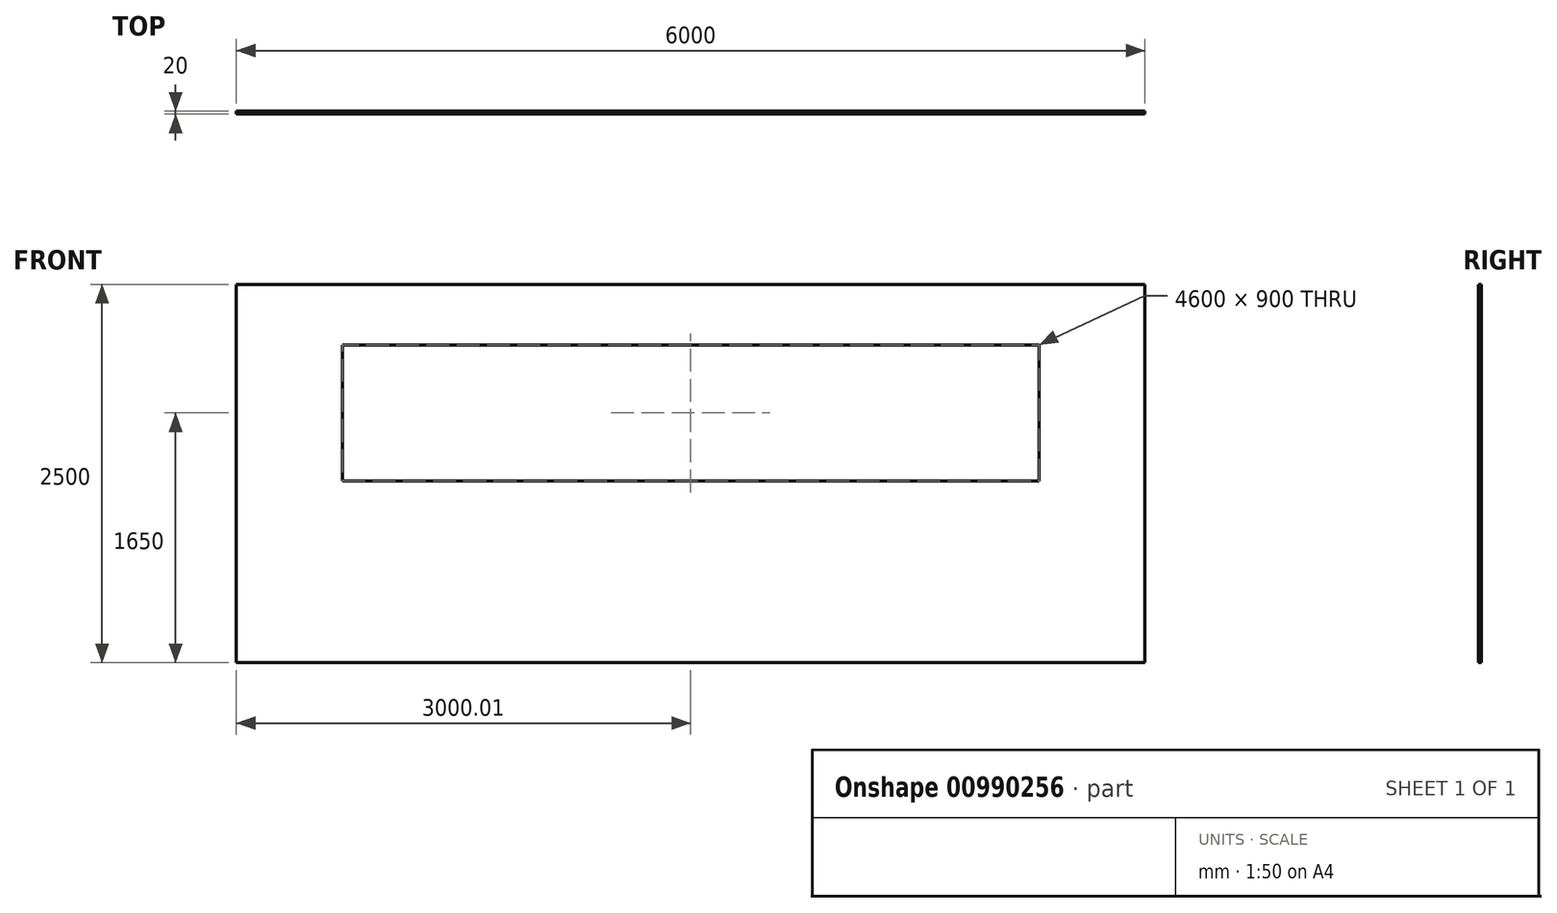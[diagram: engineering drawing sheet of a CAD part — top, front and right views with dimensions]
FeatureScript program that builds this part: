
annotation { "Feature Type Name" : "Feature", "Feature Type Description" : "" }
export const myFeature = defineFeature(function(context is Context, id is Id, definition is map)
    precondition{}
    {
        {
            var Q0;
            Q0=qCreatedBy(makeId("Front.planeOp"),FACE);
            var sketch = newSketch(context, id + "F0", { "sketchPlane" : qUnion([Q0])});
            skLineSegment(sketch, "E0.bottom", {"start": v(3864.31, 1300) * mm, "end": v(-2135.69, 1300) * mm});
            skLineSegment(sketch, "E0.top", {"start": v(3864.31, -1200) * mm, "end": v(-2135.69, -1200) * mm});
            skLineSegment(sketch, "E0.left", {"start": v(3864.31, 1300) * mm, "end": v(3864.31, -1200) * mm});
            skLineSegment(sketch, "E0.right", {"start": v(-2135.69, 1300) * mm, "end": v(-2135.69, -1200) * mm});
            skLineSegment(sketch, "E1.bottom", {"start": v(3164.31, 0) * mm, "end": v(-1435.69, 0) * mm});
            skLineSegment(sketch, "E1.top", {"start": v(3164.31, 900) * mm, "end": v(-1435.69, 900) * mm});
            skLineSegment(sketch, "E1.left", {"start": v(3164.31, 0) * mm, "end": v(3164.31, 900) * mm});
            skLineSegment(sketch, "E1.right", {"start": v(-1435.69, 0) * mm, "end": v(-1435.69, 900) * mm});
            skSolve(sketch);
        }
        {
            var Q0;
            Q0=makeQuery(id+"F0.imprint","IMPRINT",FACE,{"disambiguationData":[TD([[makeQuery(id+"F0.imprint","IMPRINT",EDGE,{"derivedFrom":sQuery(id+"F0.wireOp",EDGE,"E0.bottom")}),1.0]])]});
            extrude(context, id + "F1", {"entities" : qUnion([Q0]), "depth" : 20 * mm, "offsetDistance" : 25 * mm});
        }
    });
